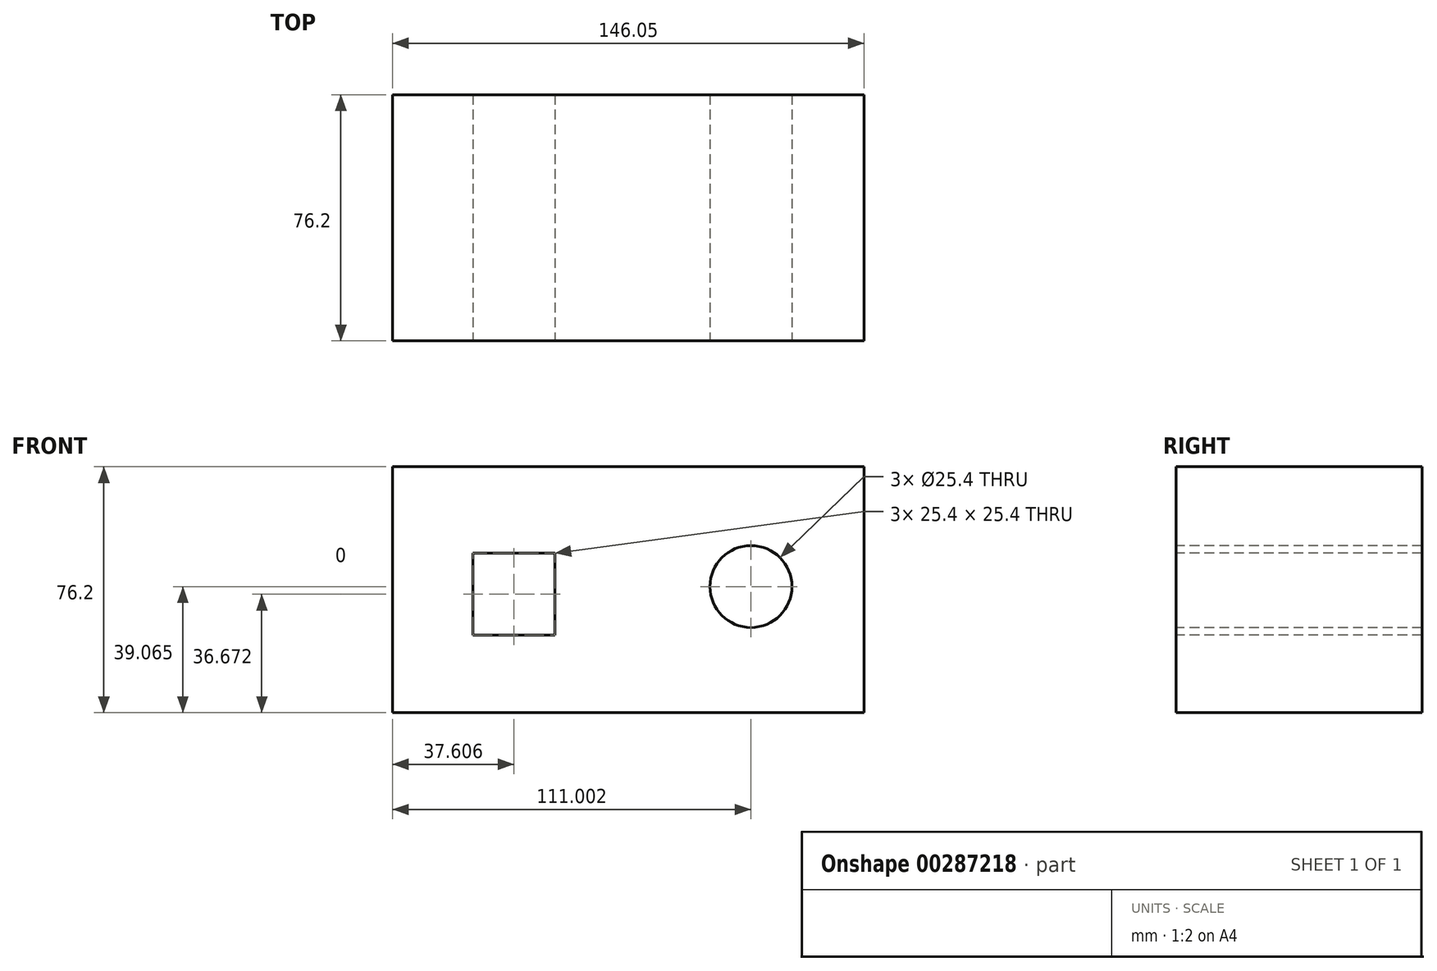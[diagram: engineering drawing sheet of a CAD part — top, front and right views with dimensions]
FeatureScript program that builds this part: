
annotation { "Feature Type Name" : "Feature", "Feature Type Description" : "" }
export const myFeature = defineFeature(function(context is Context, id is Id, definition is map)
    precondition{}
    {
        {
            var Q0;
            Q0=qCreatedBy(makeId("Front.planeOp"),FACE);
            var sketch = newSketch(context, id + "F0", { "sketchPlane" : qUnion([Q0])});
            skLineSegment(sketch, "E0.bottom", {"start": v(0, 0) * mm, "end": v(-146.05, 0) * mm});
            skLineSegment(sketch, "E0.top", {"start": v(0, 76.2) * mm, "end": v(-146.05, 76.2) * mm});
            skLineSegment(sketch, "E0.left", {"start": v(0, 0) * mm, "end": v(0, 76.2) * mm});
            skLineSegment(sketch, "E0.right", {"start": v(-146.05, 0) * mm, "end": v(-146.05, 76.2) * mm});
            skSolve(sketch);
        }
        {
            var Q0;
            Q0 = qSketchRegion(id + "F0", true);
            extrude(context, id + "F1", {"entities" : qUnion([Q0]), "depth" : 76.2 * mm});
        }
        {
            var Q0;
            Q0=makeQuery(id+"F1.opExtrude","CAP_FACE",FACE,{"disambiguationData":[OSD([sQuery(id+"F0.wireOp",EDGE,"E0.bottom"),sQuery(id+"F0.wireOp",EDGE,"E0.top"),sQuery(id+"F0.wireOp",EDGE,"E0.left"),sQuery(id+"F0.wireOp",EDGE,"E0.right")])],"isStart":false});
            var sketch = newSketch(context, id + "F2", { "sketchPlane" : qUnion([Q0])});
            skCircle(sketch, "E1", {"center": v(-35.05, 39.07) * mm, "radius": 12.7 * mm});
            skLineSegment(sketch, "E2.bottom", {"start": v(-121.14, 49.37) * mm, "end": v(-95.74, 49.37) * mm});
            skLineSegment(sketch, "E2.top", {"start": v(-121.14, 23.97) * mm, "end": v(-95.74, 23.97) * mm});
            skLineSegment(sketch, "E2.left", {"start": v(-121.14, 49.37) * mm, "end": v(-121.14, 23.97) * mm});
            skLineSegment(sketch, "E2.right", {"start": v(-95.74, 49.37) * mm, "end": v(-95.74, 23.97) * mm});
            skSolve(sketch);
        }
        {
            var Q0;
            Q0 = qSketchRegion(id + "F2", true);
            extrude(context, id + "F3", {"entities" : qUnion([Q0]), "operationType" : NewBodyOperationType.REMOVE, "oppositeDirection" : true, "depth" : 76.2 * mm});
        }
    });
